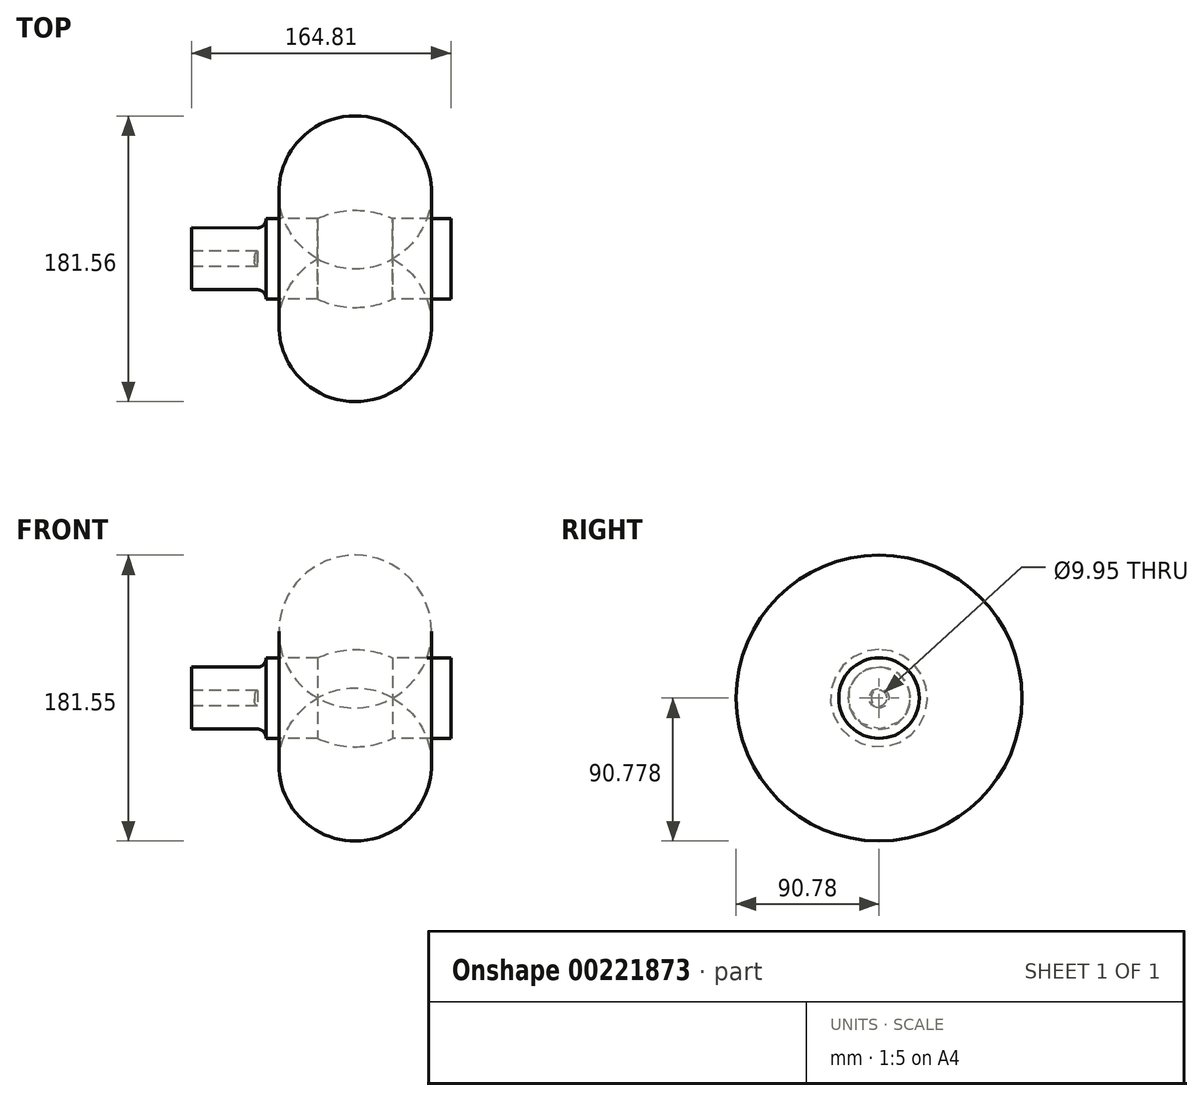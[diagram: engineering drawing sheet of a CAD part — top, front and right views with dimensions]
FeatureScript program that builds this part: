
annotation { "Feature Type Name" : "Feature", "Feature Type Description" : "" }
export const myFeature = defineFeature(function(context is Context, id is Id, definition is map)
    precondition{}
    {
        {
            var Q0;
            Q0=qCreatedBy(makeId("Front.planeOp"),FACE);
            var sketch = newSketch(context, id + "F0", { "sketchPlane" : qUnion([Q0])});
            skLineSegment(sketch, "E0", {"start": v(-71.3, 15.66) * mm, "end": v(-38.38, 15.66) * mm});
            skLineSegment(sketch, "E1", {"start": v(9.22, 15.66) * mm, "end": v(46.16, 15.66) * mm});
            skLineSegment(sketch, "E2", {"start": v(-71.3, -9.91) * mm, "end": v(-38.38, -9.91) * mm});
            skLineSegment(sketch, "E3", {"start": v(9.22, -9.91) * mm, "end": v(46.16, -9.91) * mm});
            skArc(sketch, "E4", {"start": v(9.22, 15.66) * mm, "mid": v(-14.58, 20.95) * mm, "end": v(-38.38, 15.66) * mm});
            skArc(sketch, "E5", {"start": v(-38.38, -9.91) * mm, "mid": v(-14.58, -16.15) * mm, "end": v(9.22, -9.91) * mm});
            skArc(sketch, "E6", {"start": v(-76.74, 9.74) * mm, "mid": v(-72.71, 11.5) * mm, "end": v(-71.3, 15.66) * mm});
            skArc(sketch, "E7", {"start": v(-71.3, -9.91) * mm, "mid": v(-72.14, -5.38) * mm, "end": v(-76.74, -4.94) * mm});
            skLineSegment(sketch, "E8", {"start": v(-76.74, 9.74) * mm, "end": v(-118.65, 9.78) * mm});
            skLineSegment(sketch, "E9", {"start": v(-76.74, -4.94) * mm, "end": v(-118.65, -4.94) * mm});
            skLineSegment(sketch, "E10", {"start": v(-118.65, -4.94) * mm, "end": v(-118.65, 9.78) * mm});
            skLineSegment(sketch, "E11", {"start": v(46.16, 15.66) * mm, "end": v(46.16, -9.91) * mm});
            skSolve(sketch);
        }
        {
            var Q0;
            Q0 = qSketchRegion(id + "F0", true);
            var Q1;
            Q1=sQuery(id+"F0.wireOp",EDGE,"E2");
            revolve(context, id + "F1", {"entities" : qUnion([Q0]), "axis" : qUnion([Q1]), "revolveType" : RevolveType.FULL});
        }
    });
